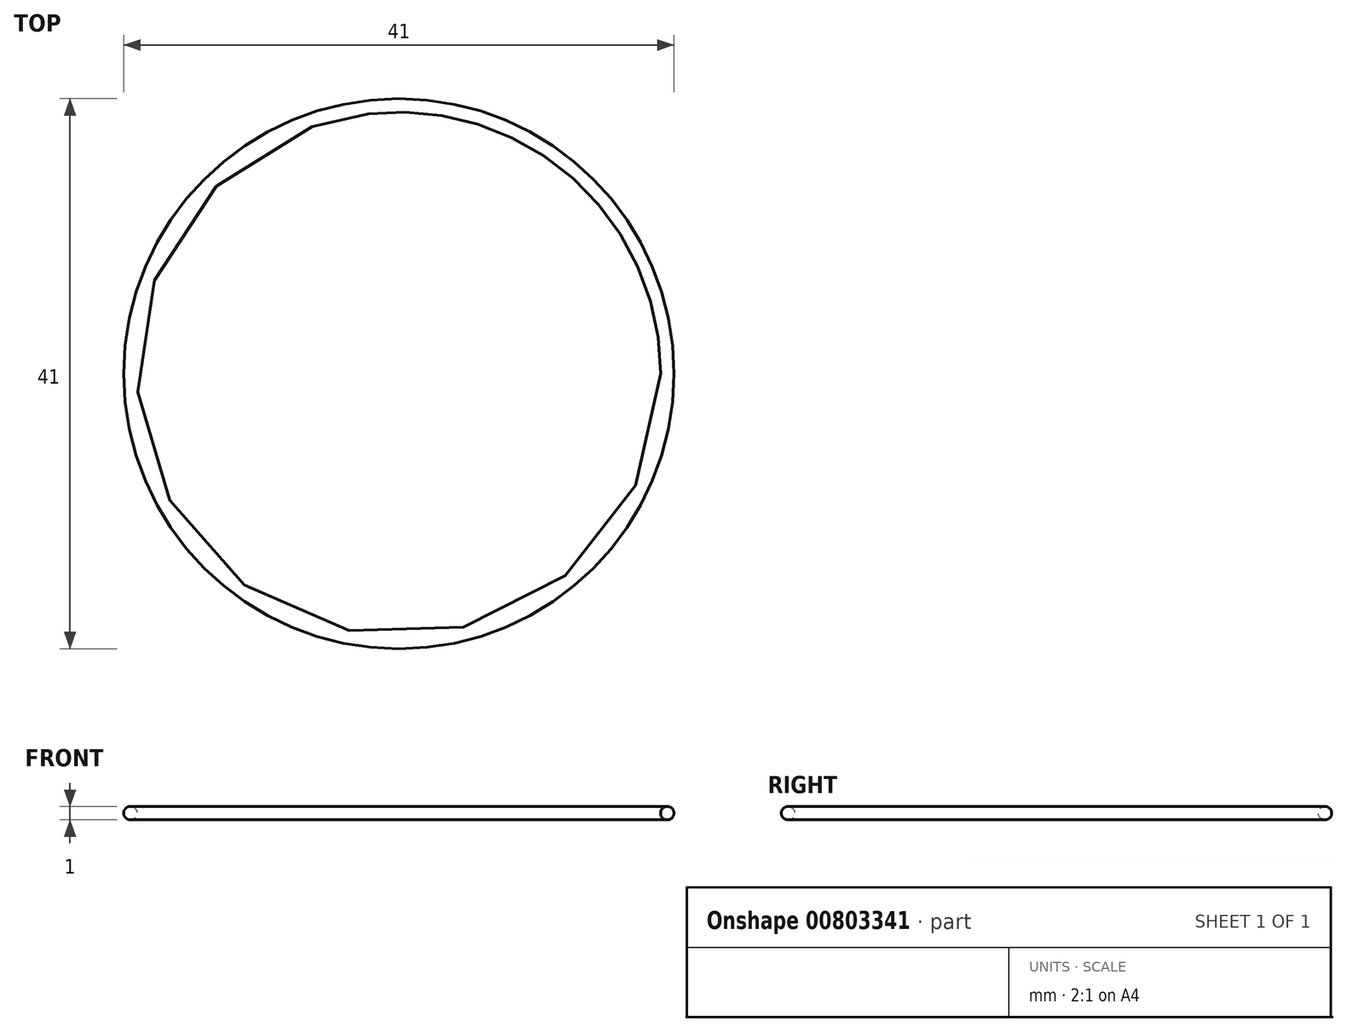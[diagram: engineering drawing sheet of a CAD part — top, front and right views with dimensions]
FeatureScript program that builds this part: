
annotation { "Feature Type Name" : "Feature", "Feature Type Description" : "" }
export const myFeature = defineFeature(function(context is Context, id is Id, definition is map)
    precondition{}
    {
        {
            var Q0;
            Q0=qCreatedBy(makeId("Front.planeOp"),FACE);
            var sketch = newSketch(context, id + "F0", { "sketchPlane" : qUnion([Q0])});
            skCircle(sketch, "E0", {"center": v(20, 0) * mm, "radius": 0.5 * mm});
            skLineSegment(sketch, "E1", {"start": v(0, 5.43) * mm, "end": v(0, -7.22) * mm});
            skSolve(sketch);
        }
        {
            var Q0;
            Q0=makeQuery(id+"F0.imprint","IMPRINT",FACE,{"disambiguationData":[TD([[makeQuery(id+"F0.imprint","IMPRINT",EDGE,{"derivedFrom":sQuery(id+"F0.wireOp",EDGE,"E0")}),1.0]])]});
            var Q1;
            Q1=sQuery(id+"F0.wireOp",EDGE,"E1");
            revolve(context, id + "F1", {"surfaceOperationType" : NewSurfaceOperationType.NEW, "entities" : qUnion([Q0]), "axis" : qUnion([Q1]), "revolveType" : RevolveType.FULL});
        }
    });
